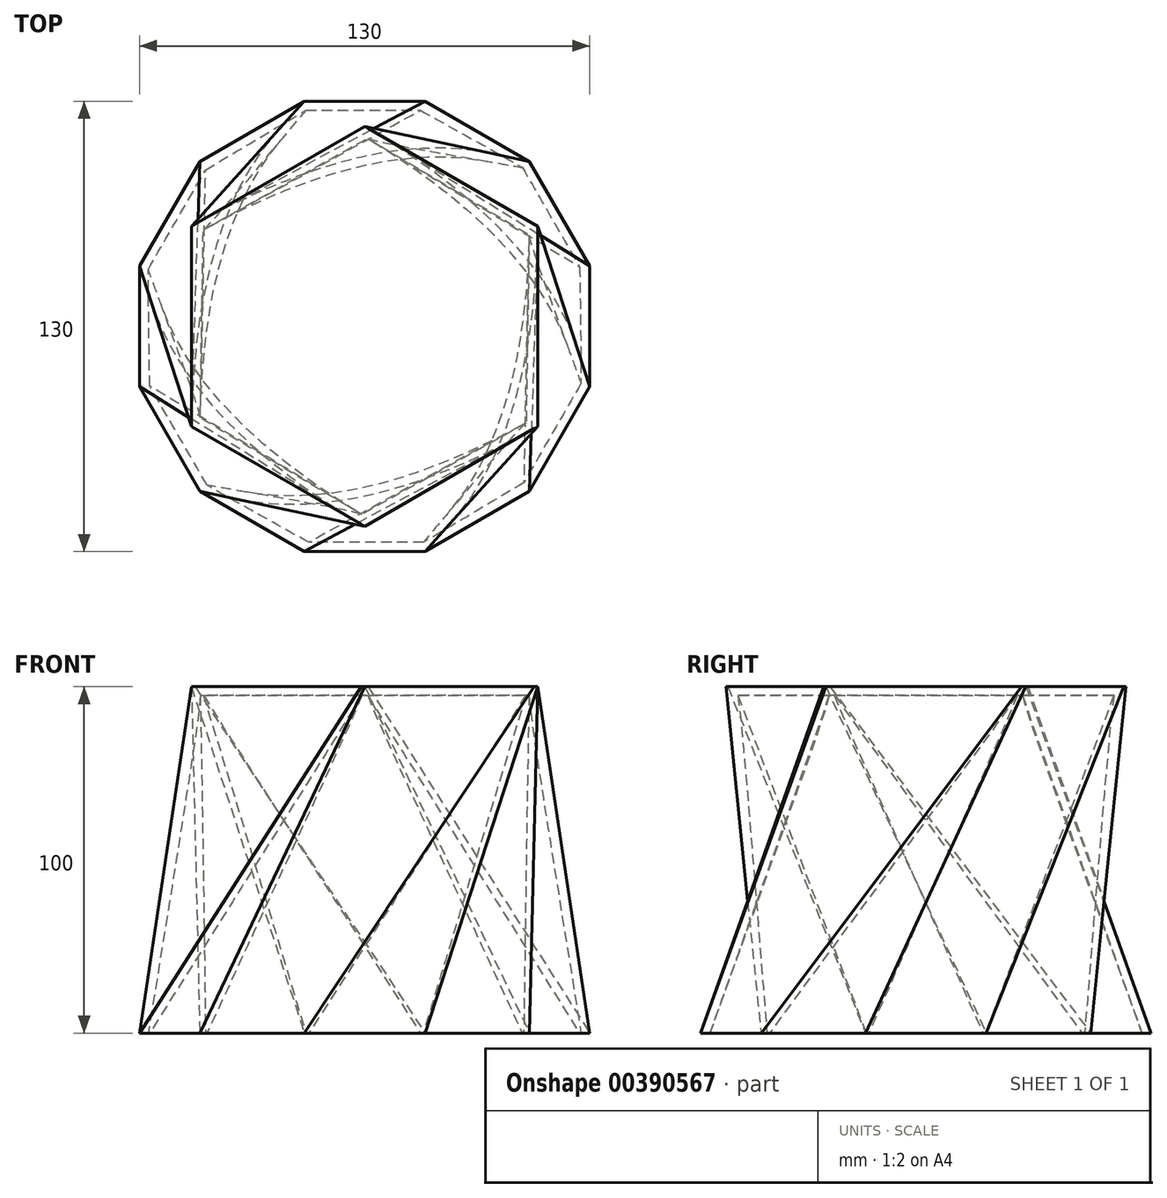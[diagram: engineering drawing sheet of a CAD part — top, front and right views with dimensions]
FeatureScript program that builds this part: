
annotation { "Feature Type Name" : "Feature", "Feature Type Description" : "" }
export const myFeature = defineFeature(function(context is Context, id is Id, definition is map)
    precondition{}
    {
        {
            var Q0;
            Q0=qCreatedBy(makeId("Top.planeOp"),FACE);
            var sketch = newSketch(context, id + "F0", { "sketchPlane" : qUnion([Q0])});
            skCircle(sketch, "E0.cCircle", {"center": v(0, 0) * mm, "radius": 50 * mm, "construction": true});
            skLineSegment(sketch, "E0.0", {"start": v(-50, -28.87) * mm, "end": v(-50, -27.72) * mm});
            skLineSegment(sketch, "E0.1", {"start": v(-50, 28.87) * mm, "end": v(-49, 29.44) * mm});
            skLineSegment(sketch, "E0.2", {"start": v(0, 57.74) * mm, "end": v(1, 57.16) * mm});
            skLineSegment(sketch, "E0.3", {"start": v(50, 28.87) * mm, "end": v(50, 27.72) * mm});
            skLineSegment(sketch, "E0.4", {"start": v(50, -28.87) * mm, "end": v(49, -29.44) * mm});
            skLineSegment(sketch, "E0.5", {"start": v(0, -57.74) * mm, "end": v(-1, -57.16) * mm});
            skLineSegment(sketch, "E1", {"start": v(-49, 29.44) * mm, "end": v(0, 57.74) * mm});
            skLineSegment(sketch, "E2", {"start": v(1, 57.16) * mm, "end": v(50, 28.87) * mm});
            skLineSegment(sketch, "E3", {"start": v(50, 27.72) * mm, "end": v(50, -28.87) * mm});
            skLineSegment(sketch, "E4", {"start": v(49, -29.44) * mm, "end": v(0, -57.74) * mm});
            skLineSegment(sketch, "E5", {"start": v(-1, -57.16) * mm, "end": v(-50, -28.87) * mm});
            skLineSegment(sketch, "E6", {"start": v(-50, -27.72) * mm, "end": v(-50, 28.87) * mm});
            skLineSegment(sketch, "E7", {"start": v(0, 0) * mm, "end": v(0, 57.74) * mm, "construction": true});
            skLineSegment(sketch, "E8", {"start": v(0, 0) * mm, "end": v(50, 28.87) * mm, "construction": true});
            skLineSegment(sketch, "E9", {"start": v(0, 0) * mm, "end": v(50, 27.72) * mm, "construction": true});
            skLineSegment(sketch, "E10", {"start": v(0, 0) * mm, "end": v(50, -28.87) * mm, "construction": true});
            skLineSegment(sketch, "E11", {"start": v(0, 0) * mm, "end": v(49, -29.44) * mm, "construction": true});
            skLineSegment(sketch, "E12", {"start": v(0, 0) * mm, "end": v(0, -57.74) * mm, "construction": true});
            skLineSegment(sketch, "E13", {"start": v(0, 0) * mm, "end": v(-1, -57.16) * mm, "construction": true});
            skLineSegment(sketch, "E14", {"start": v(0, 0) * mm, "end": v(-50, -28.87) * mm, "construction": true});
            skLineSegment(sketch, "E15", {"start": v(0, 0) * mm, "end": v(-50, -27.72) * mm, "construction": true});
            skLineSegment(sketch, "E16", {"start": v(0, 0) * mm, "end": v(-50, 28.87) * mm, "construction": true});
            skLineSegment(sketch, "E17", {"start": v(0, 0) * mm, "end": v(-49, 29.44) * mm, "construction": true});
            skLineSegment(sketch, "E18", {"start": v(0, 0) * mm, "end": v(1, 57.16) * mm, "construction": true});
            skSolve(sketch);
        }
        {
            var Q0;
            Q0=qCreatedBy(makeId("Top.planeOp"),FACE);
            cPlane(context, id + "F1", {"entities" : qUnion([Q0]), "cplaneType" : CPlaneType.OFFSET, "offset" : 100 * mm, "oppositeDirection" : true, "width" : 150 * mm, "height" : 150 * mm});
        }
        {
            var Q0;
            Q0=qCreatedBy(id+"F1.planeOp",FACE);
            var sketch = newSketch(context, id + "F2", { "sketchPlane" : qUnion([Q0])});
            skCircle(sketch, "E19.cCircle", {"center": v(0, 0) * mm, "radius": 65 * mm, "construction": true});
            skLineSegment(sketch, "E19.0", {"start": v(17.42, -65) * mm, "end": v(-17.42, -65) * mm});
            skLineSegment(sketch, "E19.1", {"start": v(-17.42, -65) * mm, "end": v(-47.58, -47.58) * mm});
            skLineSegment(sketch, "E19.2", {"start": v(-47.58, -47.58) * mm, "end": v(-65, -17.42) * mm});
            skLineSegment(sketch, "E19.3", {"start": v(-65, -17.42) * mm, "end": v(-65, 17.42) * mm});
            skLineSegment(sketch, "E19.4", {"start": v(-65, 17.42) * mm, "end": v(-47.58, 47.58) * mm});
            skLineSegment(sketch, "E19.5", {"start": v(-47.58, 47.58) * mm, "end": v(-17.42, 65) * mm});
            skLineSegment(sketch, "E19.6", {"start": v(-17.42, 65) * mm, "end": v(17.42, 65) * mm});
            skLineSegment(sketch, "E19.7", {"start": v(17.42, 65) * mm, "end": v(47.58, 47.58) * mm});
            skLineSegment(sketch, "E19.8", {"start": v(47.58, 47.58) * mm, "end": v(65, 17.42) * mm});
            skLineSegment(sketch, "E19.9", {"start": v(65, 17.42) * mm, "end": v(65, -17.42) * mm});
            skLineSegment(sketch, "E19.10", {"start": v(65, -17.42) * mm, "end": v(47.58, -47.58) * mm});
            skLineSegment(sketch, "E19.11", {"start": v(47.58, -47.58) * mm, "end": v(17.42, -65) * mm});
            skPoint(sketch, "E19.0.midPoint", {"position": v(0, -65) * mm});
            skSolve(sketch);
        }
        {
            var Q0;
            Q0=makeQuery(id+"F0.imprint","IMPRINT",FACE,{"disambiguationData":[TD([[makeQuery(id+"F0.imprint","IMPRINT",EDGE,{"derivedFrom":sQuery(id+"F0.wireOp",EDGE,"E0.0")}),-1.0]])]});
            var Q1;
            Q1=makeQuery(id+"F2.imprint","IMPRINT",FACE,{"disambiguationData":[TD([[makeQuery(id+"F2.imprint","IMPRINT",EDGE,{"derivedFrom":sQuery(id+"F2.wireOp",EDGE,"E19.0")}),-1.0]])]});
            var Q2;
            Q2=sQuery(id+"F0.wireOp",VERTEX,"E0.5.start");
            var Q3;
            Q3=sQuery(id+"F2.wireOp",VERTEX,"E19.2.start");
            loft(context, id + "F3", {"sheetProfilesArray" : [{ "sheetProfileEntities" : qUnion([Q0]) }, { "sheetProfileEntities" : qUnion([Q1]) }], "matchConnections" : true, "connections" : [{ "connectionEntities" : qUnion([Q2, Q3]), "connectionEdgeQueries" : qUnion([]), "connectionEdgeParameters" : [] }]});
        }
        {
            var Q0;
            Q0=makeQuery(id+"F3.opLoft","CAP_FACE",FACE,{"disambiguationData":[OSD([makeQuery(id+"F2.imprint","IMPRINT",FACE,{"disambiguationData":[TD([[makeQuery(id+"F2.imprint","IMPRINT",EDGE,{"derivedFrom":sQuery(id+"F2.wireOp",EDGE,"E19.0")}),-1.0]])]})])],"isStart":true});
            shell(context, id + "F4", {"entities" : qUnion([Q0]), "thickness" : 2.5 * mm});
        }
    });
